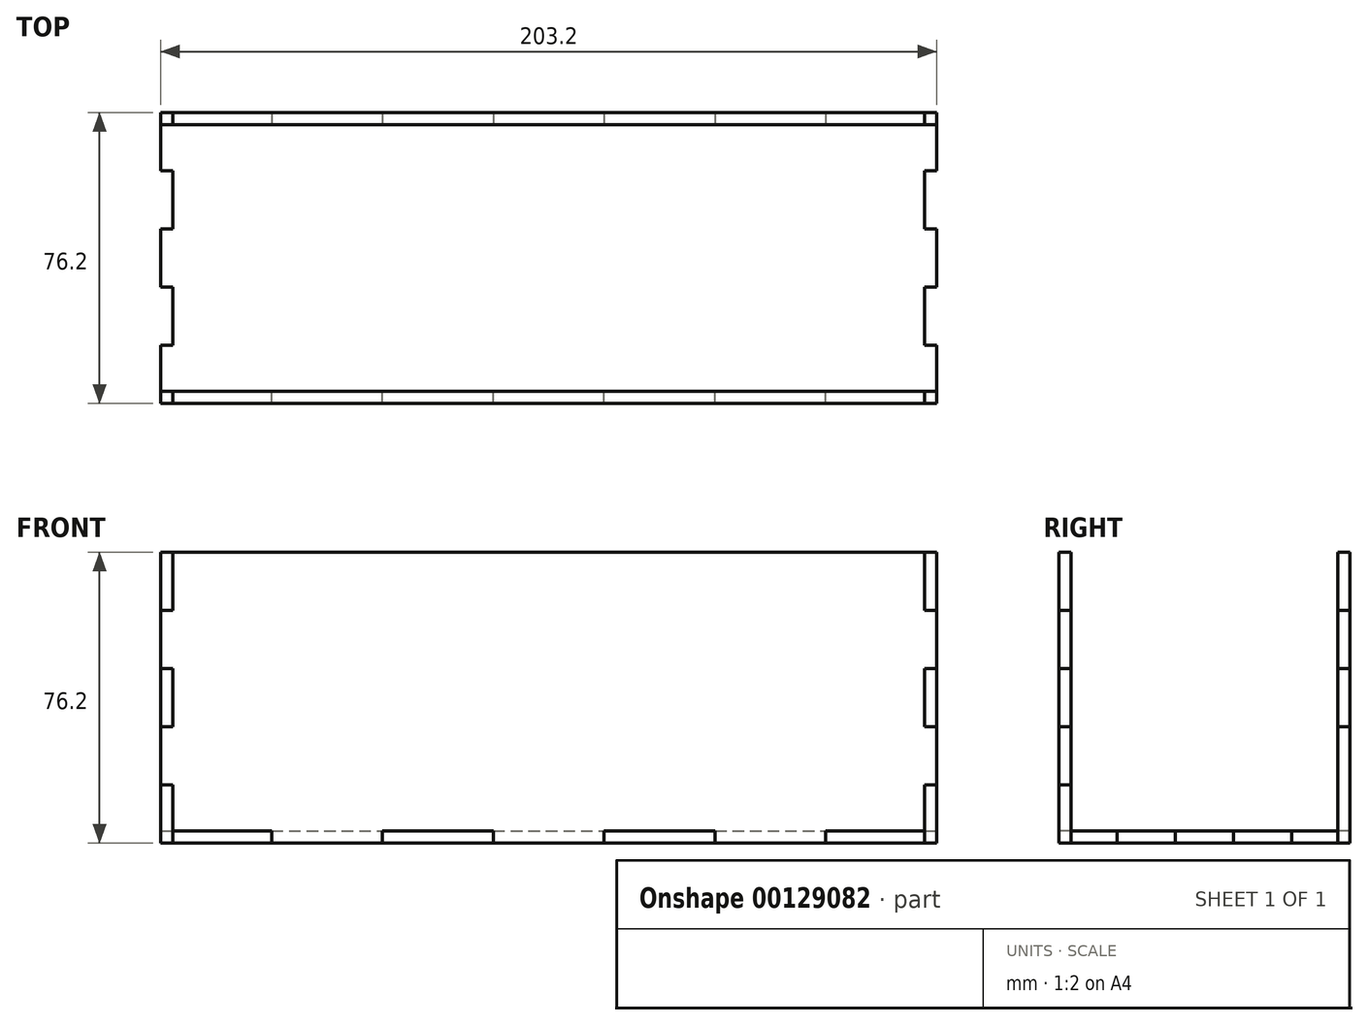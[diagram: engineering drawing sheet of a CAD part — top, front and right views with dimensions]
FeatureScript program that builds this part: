
annotation { "Feature Type Name" : "Feature", "Feature Type Description" : "" }
export const myFeature = defineFeature(function(context is Context, id is Id, definition is map)
    precondition{}
    {
        {
            var Q0;
            Q0=qCreatedBy(makeId("Top.planeOp"),FACE);
            var sketch = newSketch(context, id + "F0", { "sketchPlane" : qUnion([Q0])});
            skLineSegment(sketch, "E0.bottom", {"start": v(101.6, 38.1) * mm, "end": v(-101.6, 38.1) * mm});
            skLineSegment(sketch, "E0.top", {"start": v(101.6, -38.1) * mm, "end": v(-101.6, -38.1) * mm});
            skLineSegment(sketch, "E0.left", {"start": v(101.6, 38.1) * mm, "end": v(101.6, -38.1) * mm});
            skLineSegment(sketch, "E0.right", {"start": v(-101.6, 38.1) * mm, "end": v(-101.6, -38.1) * mm});
            skPoint(sketch, "E0.middle", {"position": v(0, 0) * mm});
            skLineSegment(sketch, "E1", {"start": v(-101.6, 38.1) * mm, "end": v(-98.43, 38.1) * mm});
            skLineSegment(sketch, "E2.0.1.0", {"start": v(-101.6, 22.86) * mm, "end": v(-98.43, 22.86) * mm});
            skLineSegment(sketch, "E2.0.2.0", {"start": v(-101.6, 7.62) * mm, "end": v(-98.43, 7.62) * mm});
            skLineSegment(sketch, "E2.0.3.0", {"start": v(-101.6, -7.62) * mm, "end": v(-98.43, -7.62) * mm});
            skLineSegment(sketch, "E2.0.4.0", {"start": v(-101.6, -22.86) * mm, "end": v(-98.43, -22.86) * mm});
            skLineSegment(sketch, "E2.0.5.0", {"start": v(-101.6, -38.1) * mm, "end": v(-98.43, -38.1) * mm});
            skLineSegment(sketch, "E2.direction1", {"start": v(-101.6, 38.1) * mm, "end": v(-50.8, 38.1) * mm, "construction": true});
            skLineSegment(sketch, "E2.direction2", {"start": v(-101.6, 38.1) * mm, "end": v(-101.6, 22.86) * mm, "construction": true});
            skLineSegment(sketch, "E3", {"start": v(-98.43, 38.1) * mm, "end": v(-98.43, -38.1) * mm});
            skLineSegment(sketch, "E4.MirrorCS", {"start": v(101.6, 38.1) * mm, "end": v(98.43, 38.1) * mm});
            skLineSegment(sketch, "E5.MirrorCS", {"start": v(101.6, -38.1) * mm, "end": v(98.43, -38.1) * mm});
            skLineSegment(sketch, "E6.MirrorCS", {"start": v(101.6, 22.86) * mm, "end": v(98.43, 22.86) * mm});
            skLineSegment(sketch, "E7.MirrorCS", {"start": v(101.6, 7.62) * mm, "end": v(98.43, 7.62) * mm});
            skLineSegment(sketch, "E8.MirrorCS", {"start": v(101.6, -7.62) * mm, "end": v(98.43, -7.62) * mm});
            skLineSegment(sketch, "E9.MirrorCS", {"start": v(101.6, -22.86) * mm, "end": v(98.43, -22.86) * mm});
            skLineSegment(sketch, "E10.MirrorCS", {"start": v(98.43, 38.1) * mm, "end": v(98.43, -38.1) * mm});
            skLineSegment(sketch, "E11.MirrorCS", {"start": v(101.6, 38.1) * mm, "end": v(101.6, 22.86) * mm, "construction": true});
            skLineSegment(sketch, "E12", {"start": v(-101.6, 38.1) * mm, "end": v(-101.6, 34.93) * mm});
            skLineSegment(sketch, "E13.1.0.0", {"start": v(-72.57, 38.1) * mm, "end": v(-72.57, 34.93) * mm});
            skLineSegment(sketch, "E13.2.0.0", {"start": v(-43.54, 38.1) * mm, "end": v(-43.54, 34.93) * mm});
            skLineSegment(sketch, "E13.3.0.0", {"start": v(-14.51, 38.1) * mm, "end": v(-14.51, 34.93) * mm});
            skLineSegment(sketch, "E13.4.0.0", {"start": v(14.51, 38.1) * mm, "end": v(14.51, 34.93) * mm});
            skLineSegment(sketch, "E13.5.0.0", {"start": v(43.54, 38.1) * mm, "end": v(43.54, 34.93) * mm});
            skLineSegment(sketch, "E13.6.0.0", {"start": v(72.57, 38.1) * mm, "end": v(72.57, 34.93) * mm});
            skLineSegment(sketch, "E13.7.0.0", {"start": v(101.6, 38.1) * mm, "end": v(101.6, 34.93) * mm});
            skLineSegment(sketch, "E13.direction1", {"start": v(-101.6, 34.92) * mm, "end": v(-72.57, 34.92) * mm, "construction": true});
            skLineSegment(sketch, "E14", {"start": v(-101.6, 34.92) * mm, "end": v(101.6, 34.93) * mm});
            skLineSegment(sketch, "E15.MirrorCS", {"start": v(-101.6, -38.1) * mm, "end": v(-101.6, -34.93) * mm});
            skLineSegment(sketch, "E16.MirrorCS", {"start": v(101.6, -38.1) * mm, "end": v(101.6, -34.93) * mm});
            skLineSegment(sketch, "E17.MirrorCS", {"start": v(-72.57, -38.1) * mm, "end": v(-72.57, -34.93) * mm});
            skLineSegment(sketch, "E18.MirrorCS", {"start": v(-14.51, -38.1) * mm, "end": v(-14.51, -34.93) * mm});
            skLineSegment(sketch, "E19.MirrorCS", {"start": v(43.54, -38.1) * mm, "end": v(43.54, -34.93) * mm});
            skLineSegment(sketch, "E20.MirrorCS", {"start": v(14.51, -38.1) * mm, "end": v(14.51, -34.93) * mm});
            skLineSegment(sketch, "E21.MirrorCS", {"start": v(-43.54, -38.1) * mm, "end": v(-43.54, -34.93) * mm});
            skLineSegment(sketch, "E22.MirrorCS", {"start": v(72.57, -38.1) * mm, "end": v(72.57, -34.93) * mm});
            skLineSegment(sketch, "E23.MirrorCS", {"start": v(-101.6, -34.93) * mm, "end": v(101.6, -34.92) * mm});
            skLineSegment(sketch, "E24.MirrorCS", {"start": v(-101.6, -38.1) * mm, "end": v(-50.8, -38.1) * mm, "construction": true});
            skLineSegment(sketch, "E25.MirrorCS", {"start": v(-101.6, -34.93) * mm, "end": v(-72.57, -34.93) * mm, "construction": true});
            skSolve(sketch);
        }
        {
            var Q0;
            {var subQ0=sQuery(id+"F0.wireOp",EDGE,"E1");Q0=makeQuery(id+"F0.imprint","IMPRINT",FACE,{"disambiguationData":[TD([[makeQuery(id+"F0.imprint","IMPRINT",EDGE,{"derivedFrom":subQ0}),-1.0]])]});}
            var Q1;
            {var subQ3=sQuery(id+"F0.wireOp",EDGE,"E2.0.1.0");Q1=makeQuery(id+"F0.imprint","IMPRINT",FACE,{"disambiguationData":[TD([[makeQuery(id+"F0.imprint","IMPRINT",EDGE,{"derivedFrom":subQ3}),1.0]])]});}
            var Q2;
            {var subQ3=sQuery(id+"F0.wireOp",EDGE,"E13.1.0.0");Q2=makeQuery(id+"F0.imprint","IMPRINT",FACE,{"disambiguationData":[TD([[makeQuery(id+"F0.imprint","IMPRINT",EDGE,{"derivedFrom":subQ3}),-1.0]])]});}
            var Q3;
            {var subQ5=sQuery(id+"F0.wireOp",EDGE,"E3");var subQ23=makeQuery(id+"F0.imprint","INTERSECT",VERTEX,{"derivedFrom":[sQuery(id+"F0.wireOp",EDGE,"E2.0.1.0"),subQ5]});Q3=makeQuery(id+"F0.imprint","IMPRINT",FACE,{"disambiguationData":[TD([[makeQuery(id+"F0.imprint","IMPRINT",EDGE,{"disambiguationData":[TD([[subQ23,1.0]])],"derivedFrom":subQ5}),1.0]])]});}
            var Q4;
            {var subQ0=sQuery(id+"F0.wireOp",EDGE,"E2.0.2.0");Q4=makeQuery(id+"F0.imprint","IMPRINT",FACE,{"disambiguationData":[TD([[makeQuery(id+"F0.imprint","IMPRINT",EDGE,{"derivedFrom":subQ0}),-1.0]])]});}
            var Q5;
            {var subQ3=sQuery(id+"F0.wireOp",EDGE,"E2.0.4.0");Q5=makeQuery(id+"F0.imprint","IMPRINT",FACE,{"disambiguationData":[TD([[makeQuery(id+"F0.imprint","IMPRINT",EDGE,{"derivedFrom":subQ3}),-1.0]])]});}
            var Q6;
            {var subQ5=sQuery(id+"F0.wireOp",EDGE,"E15.MirrorCS");Q6=makeQuery(id+"F0.imprint","IMPRINT",FACE,{"disambiguationData":[TD([[makeQuery(id+"F0.imprint","IMPRINT",EDGE,{"derivedFrom":subQ5}),-1.0]])]});}
            var Q7;
            {var subQ5=sQuery(id+"F0.wireOp",EDGE,"E17.MirrorCS");Q7=makeQuery(id+"F0.imprint","IMPRINT",FACE,{"disambiguationData":[TD([[makeQuery(id+"F0.imprint","IMPRINT",EDGE,{"derivedFrom":subQ5}),1.0]])]});}
            var Q8;
            {var subQ0=sQuery(id+"F0.wireOp",EDGE,"E18.MirrorCS");Q8=makeQuery(id+"F0.imprint","IMPRINT",FACE,{"disambiguationData":[TD([[makeQuery(id+"F0.imprint","IMPRINT",EDGE,{"derivedFrom":subQ0}),1.0]])]});}
            var Q9;
            {var subQ0=sQuery(id+"F0.wireOp",EDGE,"E19.MirrorCS");Q9=makeQuery(id+"F0.imprint","IMPRINT",FACE,{"disambiguationData":[TD([[makeQuery(id+"F0.imprint","IMPRINT",EDGE,{"derivedFrom":subQ0}),1.0]])]});}
            var Q10;
            {var subQ5=sQuery(id+"F0.wireOp",EDGE,"E22.MirrorCS");Q10=makeQuery(id+"F0.imprint","IMPRINT",FACE,{"disambiguationData":[TD([[makeQuery(id+"F0.imprint","IMPRINT",EDGE,{"derivedFrom":subQ5}),-1.0]])]});}
            var Q11;
            {var subQ5=sQuery(id+"F0.wireOp",EDGE,"E16.MirrorCS");Q11=makeQuery(id+"F0.imprint","IMPRINT",FACE,{"disambiguationData":[TD([[makeQuery(id+"F0.imprint","IMPRINT",EDGE,{"derivedFrom":subQ5}),1.0]])]});}
            var Q12;
            {var subQ0=sQuery(id+"F0.wireOp",EDGE,"E9.MirrorCS");Q12=makeQuery(id+"F0.imprint","IMPRINT",FACE,{"disambiguationData":[TD([[makeQuery(id+"F0.imprint","IMPRINT",EDGE,{"derivedFrom":subQ0}),1.0]])]});}
            var Q13;
            {var subQ0=sQuery(id+"F0.wireOp",EDGE,"E7.MirrorCS");Q13=makeQuery(id+"F0.imprint","IMPRINT",FACE,{"disambiguationData":[TD([[makeQuery(id+"F0.imprint","IMPRINT",EDGE,{"derivedFrom":subQ0}),1.0]])]});}
            var Q14;
            {var subQ0=sQuery(id+"F0.wireOp",EDGE,"E6.MirrorCS");Q14=makeQuery(id+"F0.imprint","IMPRINT",FACE,{"disambiguationData":[TD([[makeQuery(id+"F0.imprint","IMPRINT",EDGE,{"derivedFrom":subQ0}),-1.0]])]});}
            var Q15;
            {var subQ0=sQuery(id+"F0.wireOp",EDGE,"E4.MirrorCS");Q15=makeQuery(id+"F0.imprint","IMPRINT",FACE,{"disambiguationData":[TD([[makeQuery(id+"F0.imprint","IMPRINT",EDGE,{"derivedFrom":subQ0}),1.0]])]});}
            var Q16;
            {var subQ3=sQuery(id+"F0.wireOp",EDGE,"E13.6.0.0");Q16=makeQuery(id+"F0.imprint","IMPRINT",FACE,{"disambiguationData":[TD([[makeQuery(id+"F0.imprint","IMPRINT",EDGE,{"derivedFrom":subQ3}),1.0]])]});}
            var Q17;
            {var subQ0=sQuery(id+"F0.wireOp",EDGE,"E13.4.0.0");Q17=makeQuery(id+"F0.imprint","IMPRINT",FACE,{"disambiguationData":[TD([[makeQuery(id+"F0.imprint","IMPRINT",EDGE,{"derivedFrom":subQ0}),1.0]])]});}
            var Q18;
            {var subQ0=sQuery(id+"F0.wireOp",EDGE,"E13.2.0.0");Q18=makeQuery(id+"F0.imprint","IMPRINT",FACE,{"disambiguationData":[TD([[makeQuery(id+"F0.imprint","IMPRINT",EDGE,{"derivedFrom":subQ0}),1.0]])]});}
            extrude(context, id + "F1", {"entities" : qUnion([Q0, Q1, Q2, Q3, Q4, Q5, Q6, Q7, Q8, Q9, Q10, Q11, Q12, Q13, Q14, Q15, Q16, Q17, Q18]), "depth" : 3.17 * mm});
        }
        {
            var Q0;
            Q0=makeQuery(id+"F1.opExtrude","SWEPT_FACE",FACE,{"disambiguationData":[OSD([sQuery(id+"F0.wireOp",EDGE,"E0.left"),sQuery(id+"F0.wireOp",EDGE,"E16.MirrorCS")])]});
            var sketch = newSketch(context, id + "F2", { "sketchPlane" : qUnion([Q0])});
            skLineSegment(sketch, "E26.bottom", {"start": v(-38.1, 0) * mm, "end": v(38.1, 0) * mm});
            skLineSegment(sketch, "E26.top", {"start": v(-38.1, 76.2) * mm, "end": v(38.1, 76.2) * mm});
            skLineSegment(sketch, "E26.left", {"start": v(-38.1, 0) * mm, "end": v(-38.1, 76.2) * mm});
            skLineSegment(sketch, "E26.right", {"start": v(38.1, 0) * mm, "end": v(38.1, 76.2) * mm});
            skLineSegment(sketch, "E27", {"start": v(-38.1, 76.2) * mm, "end": v(-34.93, 76.2) * mm});
            skLineSegment(sketch, "E28.0.1.0", {"start": v(-38.1, 60.96) * mm, "end": v(-34.93, 60.96) * mm});
            skLineSegment(sketch, "E28.0.2.0", {"start": v(-38.1, 45.72) * mm, "end": v(-34.93, 45.72) * mm});
            skLineSegment(sketch, "E28.0.3.0", {"start": v(-38.1, 30.48) * mm, "end": v(-34.93, 30.48) * mm});
            skLineSegment(sketch, "E28.0.4.0", {"start": v(-38.1, 15.24) * mm, "end": v(-34.93, 15.24) * mm});
            skLineSegment(sketch, "E28.0.5.0", {"start": v(-38.1, 0) * mm, "end": v(-34.93, 0) * mm});
            skLineSegment(sketch, "E28.direction1", {"start": v(-38.1, 76.2) * mm, "end": v(-25.4, 76.2) * mm, "construction": true});
            skLineSegment(sketch, "E28.direction2", {"start": v(-38.1, 76.2) * mm, "end": v(-38.1, 60.96) * mm, "construction": true});
            skLineSegment(sketch, "E29", {"start": v(-34.93, 76.2) * mm, "end": v(-34.93, 0) * mm});
            skLineSegment(sketch, "E30.MirrorCS", {"start": v(38.1, 76.2) * mm, "end": v(34.92, 76.2) * mm});
            skLineSegment(sketch, "E31.MirrorCS", {"start": v(38.1, 0) * mm, "end": v(34.93, 0) * mm});
            skLineSegment(sketch, "E32.MirrorCS", {"start": v(38.1, 60.96) * mm, "end": v(34.92, 60.96) * mm});
            skLineSegment(sketch, "E33.MirrorCS", {"start": v(38.1, 30.48) * mm, "end": v(34.93, 30.48) * mm});
            skLineSegment(sketch, "E34.MirrorCS", {"start": v(38.1, 15.24) * mm, "end": v(34.93, 15.24) * mm});
            skLineSegment(sketch, "E35.MirrorCS", {"start": v(38.1, 45.72) * mm, "end": v(34.93, 45.72) * mm});
            skLineSegment(sketch, "E36.MirrorCS", {"start": v(38.1, 76.2) * mm, "end": v(38.1, 60.96) * mm, "construction": true});
            skLineSegment(sketch, "E37.MirrorCS", {"start": v(34.93, 76.2) * mm, "end": v(34.93, 0) * mm});
            skSolve(sketch);
        }
        {
            var Q0;
            {var subQ3=sQuery(id+"F2.wireOp",EDGE,"E26.top");Q0=makeQuery(id+"F2.imprint","IMPRINT",FACE,{"disambiguationData":[TD([[makeQuery(id+"F2.imprint","IMPRINT",EDGE,{"derivedFrom":subQ3}),-1.0]])]});}
            var Q1;
            {var subQ0=sQuery(id+"F2.wireOp",EDGE,"E27");Q1=makeQuery(id+"F2.imprint","IMPRINT",FACE,{"disambiguationData":[TD([[makeQuery(id+"F2.imprint","IMPRINT",EDGE,{"derivedFrom":subQ0}),-1.0]])]});}
            var Q2;
            {var subQ0=sQuery(id+"F2.wireOp",EDGE,"E28.0.2.0");Q2=makeQuery(id+"F2.imprint","IMPRINT",FACE,{"disambiguationData":[TD([[makeQuery(id+"F2.imprint","IMPRINT",EDGE,{"derivedFrom":subQ0}),-1.0]])]});}
            var Q3;
            {var subQ3=sQuery(id+"F2.wireOp",EDGE,"E28.0.4.0");Q3=makeQuery(id+"F2.imprint","IMPRINT",FACE,{"disambiguationData":[TD([[makeQuery(id+"F2.imprint","IMPRINT",EDGE,{"derivedFrom":subQ3}),-1.0]])]});}
            var Q4;
            {var subQ0=sQuery(id+"F2.wireOp",EDGE,"E28.0.5.0");Q4=makeQuery(id+"F2.imprint","IMPRINT",FACE,{"disambiguationData":[TD([[makeQuery(id+"F2.imprint","IMPRINT",EDGE,{"derivedFrom":subQ0}),1.0]])]});}
            var Q5;
            {var subQ1=sQuery(id+"F0.wireOp",EDGE,"E0.left");var subQ2=makeQuery(id+"F1.opExtrude","SWEPT_EDGE",EDGE,{"disambiguationData":[OSD([sQuery(id+"F0.wireOp",EDGE,"E9.MirrorCS"),subQ1])]});Q5=makeQuery(id+"F2.imprint","IMPRINT",FACE,{"disambiguationData":[TD([[makeQuery(id+"F2.imprint","IMPRINT",EDGE,{"derivedFrom":subQ2}),-1.0]])]});}
            var Q6;
            {var subQ0=sQuery(id+"F2.wireOp",EDGE,"E31.MirrorCS");Q6=makeQuery(id+"F2.imprint","IMPRINT",FACE,{"disambiguationData":[TD([[makeQuery(id+"F2.imprint","IMPRINT",EDGE,{"derivedFrom":subQ0}),-1.0]])]});}
            var Q7;
            {var subQ0=sQuery(id+"F2.wireOp",EDGE,"E33.MirrorCS");Q7=makeQuery(id+"F2.imprint","IMPRINT",FACE,{"disambiguationData":[TD([[makeQuery(id+"F2.imprint","IMPRINT",EDGE,{"derivedFrom":subQ0}),-1.0]])]});}
            var Q8;
            {var subQ0=sQuery(id+"F2.wireOp",EDGE,"E30.MirrorCS");Q8=makeQuery(id+"F2.imprint","IMPRINT",FACE,{"disambiguationData":[TD([[makeQuery(id+"F2.imprint","IMPRINT",EDGE,{"derivedFrom":subQ0}),1.0]])]});}
            extrude(context, id + "F3", {"entities" : qUnion([Q0, Q1, Q2, Q3, Q4, Q5, Q6, Q7, Q8]), "oppositeDirection" : true, "depth" : 3.17 * mm});
        }
        {
            var Q0;
            Q0=makeQuery(id+"F3.opExtrude","SWEPT_BODY",BODY,{"disambiguationData":[OSD([sQuery(id+"F2.wireOp",EDGE,"E26.bottom"),sQuery(id+"F2.wireOp",EDGE,"E26.top"),sQuery(id+"F2.wireOp",EDGE,"E26.left"),sQuery(id+"F2.wireOp",EDGE,"E27"),sQuery(id+"F2.wireOp",EDGE,"E28.0.1.0"),sQuery(id+"F2.wireOp",EDGE,"E28.0.2.0"),sQuery(id+"F2.wireOp",EDGE,"E28.0.3.0"),sQuery(id+"F2.wireOp",EDGE,"E28.0.4.0"),sQuery(id+"F2.wireOp",EDGE,"E28.0.5.0"),sQuery(id+"F2.wireOp",EDGE,"E29"),sQuery(id+"F2.wireOp",EDGE,"E30.MirrorCS"),sQuery(id+"F2.wireOp",EDGE,"E31.MirrorCS"),sQuery(id+"F2.wireOp",EDGE,"E32.MirrorCS"),sQuery(id+"F2.wireOp",EDGE,"E33.MirrorCS"),sQuery(id+"F2.wireOp",EDGE,"E34.MirrorCS"),sQuery(id+"F2.wireOp",EDGE,"E35.MirrorCS"),sQuery(id+"F2.wireOp",EDGE,"E26.right"),sQuery(id+"F2.wireOp",EDGE,"E37.MirrorCS")])]});
            var Q1;
            Q1=qCreatedBy(makeId("Right.planeOp"),FACE);
            mirror(context, id + "F4", {"entities" : qUnion([Q0]), "mirrorPlane" : qUnion([Q1])});
        }
        {
            var Q0;
            Q0=makeQuery(id+"F1.opExtrude","SWEPT_BODY",BODY,{"disambiguationData":[OSD([sQuery(id+"F0.wireOp",EDGE,"E0.bottom"),sQuery(id+"F0.wireOp",EDGE,"E0.right"),sQuery(id+"F0.wireOp",EDGE,"E1"),sQuery(id+"F0.wireOp",EDGE,"E2.0.1.0"),sQuery(id+"F0.wireOp",EDGE,"E2.0.2.0"),sQuery(id+"F0.wireOp",EDGE,"E2.0.3.0"),sQuery(id+"F0.wireOp",EDGE,"E2.0.4.0"),sQuery(id+"F0.wireOp",EDGE,"E3"),sQuery(id+"F0.wireOp",EDGE,"E4.MirrorCS"),sQuery(id+"F0.wireOp",EDGE,"E6.MirrorCS"),sQuery(id+"F0.wireOp",EDGE,"E7.MirrorCS"),sQuery(id+"F0.wireOp",EDGE,"E8.MirrorCS"),sQuery(id+"F0.wireOp",EDGE,"E9.MirrorCS"),sQuery(id+"F0.wireOp",EDGE,"E10.MirrorCS"),sQuery(id+"F0.wireOp",EDGE,"E0.left"),sQuery(id+"F0.wireOp",EDGE,"E12"),sQuery(id+"F0.wireOp",EDGE,"E13.1.0.0"),sQuery(id+"F0.wireOp",EDGE,"E13.2.0.0"),sQuery(id+"F0.wireOp",EDGE,"E13.3.0.0"),sQuery(id+"F0.wireOp",EDGE,"E13.4.0.0"),sQuery(id+"F0.wireOp",EDGE,"E13.5.0.0"),sQuery(id+"F0.wireOp",EDGE,"E13.6.0.0"),sQuery(id+"F0.wireOp",EDGE,"E13.7.0.0"),sQuery(id+"F0.wireOp",EDGE,"E14"),sQuery(id+"F0.wireOp",EDGE,"E15.MirrorCS"),sQuery(id+"F0.wireOp",EDGE,"E16.MirrorCS"),sQuery(id+"F0.wireOp",EDGE,"E17.MirrorCS"),sQuery(id+"F0.wireOp",EDGE,"E18.MirrorCS"),sQuery(id+"F0.wireOp",EDGE,"E19.MirrorCS"),sQuery(id+"F0.wireOp",EDGE,"E20.MirrorCS"),sQuery(id+"F0.wireOp",EDGE,"E21.MirrorCS"),sQuery(id+"F0.wireOp",EDGE,"E22.MirrorCS"),sQuery(id+"F0.wireOp",EDGE,"E23.MirrorCS"),sQuery(id+"F0.wireOp",EDGE,"E0.top")])]});
            var Q1;
            Q1=makeQuery(id+"F3.opExtrude","SWEPT_BODY",BODY,{"disambiguationData":[OSD([sQuery(id+"F2.wireOp",EDGE,"E26.bottom"),sQuery(id+"F2.wireOp",EDGE,"E26.top"),sQuery(id+"F2.wireOp",EDGE,"E26.left"),sQuery(id+"F2.wireOp",EDGE,"E27"),sQuery(id+"F2.wireOp",EDGE,"E28.0.1.0"),sQuery(id+"F2.wireOp",EDGE,"E28.0.2.0"),sQuery(id+"F2.wireOp",EDGE,"E28.0.3.0"),sQuery(id+"F2.wireOp",EDGE,"E28.0.4.0"),sQuery(id+"F2.wireOp",EDGE,"E28.0.5.0"),sQuery(id+"F2.wireOp",EDGE,"E29"),sQuery(id+"F2.wireOp",EDGE,"E30.MirrorCS"),sQuery(id+"F2.wireOp",EDGE,"E31.MirrorCS"),sQuery(id+"F2.wireOp",EDGE,"E32.MirrorCS"),sQuery(id+"F2.wireOp",EDGE,"E33.MirrorCS"),sQuery(id+"F2.wireOp",EDGE,"E34.MirrorCS"),sQuery(id+"F2.wireOp",EDGE,"E35.MirrorCS"),sQuery(id+"F2.wireOp",EDGE,"E26.right"),sQuery(id+"F2.wireOp",EDGE,"E37.MirrorCS")])]});
            var Q2;
            Q2=makeQuery(id+"F4.opPattern","COPY",BODY,{"derivedFrom":makeQuery(id+"F3.opExtrude","SWEPT_BODY",BODY,{"disambiguationData":[OSD([sQuery(id+"F2.wireOp",EDGE,"E26.bottom"),sQuery(id+"F2.wireOp",EDGE,"E26.top"),sQuery(id+"F2.wireOp",EDGE,"E26.left"),sQuery(id+"F2.wireOp",EDGE,"E27"),sQuery(id+"F2.wireOp",EDGE,"E28.0.1.0"),sQuery(id+"F2.wireOp",EDGE,"E28.0.2.0"),sQuery(id+"F2.wireOp",EDGE,"E28.0.3.0"),sQuery(id+"F2.wireOp",EDGE,"E28.0.4.0"),sQuery(id+"F2.wireOp",EDGE,"E28.0.5.0"),sQuery(id+"F2.wireOp",EDGE,"E29"),sQuery(id+"F2.wireOp",EDGE,"E30.MirrorCS"),sQuery(id+"F2.wireOp",EDGE,"E31.MirrorCS"),sQuery(id+"F2.wireOp",EDGE,"E32.MirrorCS"),sQuery(id+"F2.wireOp",EDGE,"E33.MirrorCS"),sQuery(id+"F2.wireOp",EDGE,"E34.MirrorCS"),sQuery(id+"F2.wireOp",EDGE,"E35.MirrorCS"),sQuery(id+"F2.wireOp",EDGE,"E26.right"),sQuery(id+"F2.wireOp",EDGE,"E37.MirrorCS")])]}),"instanceName":"1"});
            booleanBodies(context, id + "F5", {"operationType" : BooleanOperationType.SUBTRACTION, "tools" : qUnion([Q0]), "targets" : qUnion([Q1, Q2]), "keepTools" : true});
        }
        {
            var Q0;
            Q0=makeQuery(id+"F1.opExtrude","SWEPT_FACE",FACE,{"disambiguationData":[OSD([sQuery(id+"F0.wireOp",EDGE,"E0.bottom"),sQuery(id+"F0.wireOp",EDGE,"E4.MirrorCS")])]});
            var sketch = newSketch(context, id + "F6", { "sketchPlane" : qUnion([Q0])});
            skLineSegment(sketch, "E38.bottom", {"start": v(-101.6, 0) * mm, "end": v(101.6, 0) * mm});
            skLineSegment(sketch, "E38.top", {"start": v(-101.6, 76.2) * mm, "end": v(101.6, 76.2) * mm});
            skLineSegment(sketch, "E38.left", {"start": v(-101.6, 0) * mm, "end": v(-101.6, 76.2) * mm});
            skLineSegment(sketch, "E38.right", {"start": v(101.6, 0) * mm, "end": v(101.6, 76.2) * mm});
            skSolve(sketch);
        }
        {
            var Q0;
            {var subQ4=sQuery(id+"F6.wireOp",EDGE,"E38.top");Q0=makeQuery(id+"F6.imprint","IMPRINT",FACE,{"disambiguationData":[TD([[makeQuery(id+"F6.imprint","IMPRINT",EDGE,{"derivedFrom":subQ4}),-1.0]])]});}
            extrude(context, id + "F7", {"entities" : qUnion([Q0]), "oppositeDirection" : true, "depth" : 3.17 * mm});
        }
        {
            var Q0;
            Q0=makeQuery(id+"F7.opExtrude","SWEPT_BODY",BODY,{"disambiguationData":[OSD([sQuery(id+"F0.wireOp",EDGE,"E0.bottom"),sQuery(id+"F0.wireOp",EDGE,"E4.MirrorCS"),sQuery(id+"F0.wireOp",EDGE,"E13.6.0.0"),sQuery(id+"F6.wireOp",EDGE,"E38.bottom"),sQuery(id+"F6.wireOp",EDGE,"E38.top"),sQuery(id+"F6.wireOp",EDGE,"E38.left"),sQuery(id+"F6.wireOp",EDGE,"E38.right")])]});
            var Q1;
            Q1=qCreatedBy(makeId("Front.planeOp"),FACE);
            mirror(context, id + "F8", {"entities" : qUnion([Q0]), "mirrorPlane" : qUnion([Q1])});
        }
        {
            var Q0;
            Q0=makeQuery(id+"F4.opPattern","COPY",BODY,{"derivedFrom":makeQuery(id+"F3.opExtrude","SWEPT_BODY",BODY,{"disambiguationData":[OSD([sQuery(id+"F2.wireOp",EDGE,"E26.bottom"),sQuery(id+"F2.wireOp",EDGE,"E26.top"),sQuery(id+"F2.wireOp",EDGE,"E26.left"),sQuery(id+"F2.wireOp",EDGE,"E27"),sQuery(id+"F2.wireOp",EDGE,"E28.0.1.0"),sQuery(id+"F2.wireOp",EDGE,"E28.0.2.0"),sQuery(id+"F2.wireOp",EDGE,"E28.0.3.0"),sQuery(id+"F2.wireOp",EDGE,"E28.0.4.0"),sQuery(id+"F2.wireOp",EDGE,"E28.0.5.0"),sQuery(id+"F2.wireOp",EDGE,"E29"),sQuery(id+"F2.wireOp",EDGE,"E30.MirrorCS"),sQuery(id+"F2.wireOp",EDGE,"E31.MirrorCS"),sQuery(id+"F2.wireOp",EDGE,"E32.MirrorCS"),sQuery(id+"F2.wireOp",EDGE,"E33.MirrorCS"),sQuery(id+"F2.wireOp",EDGE,"E34.MirrorCS"),sQuery(id+"F2.wireOp",EDGE,"E35.MirrorCS"),sQuery(id+"F2.wireOp",EDGE,"E26.right"),sQuery(id+"F2.wireOp",EDGE,"E37.MirrorCS")])]}),"instanceName":"1"});
            var Q1;
            Q1=makeQuery(id+"F1.opExtrude","SWEPT_BODY",BODY,{"disambiguationData":[OSD([sQuery(id+"F0.wireOp",EDGE,"E0.bottom"),sQuery(id+"F0.wireOp",EDGE,"E0.right"),sQuery(id+"F0.wireOp",EDGE,"E1"),sQuery(id+"F0.wireOp",EDGE,"E2.0.1.0"),sQuery(id+"F0.wireOp",EDGE,"E2.0.2.0"),sQuery(id+"F0.wireOp",EDGE,"E2.0.3.0"),sQuery(id+"F0.wireOp",EDGE,"E2.0.4.0"),sQuery(id+"F0.wireOp",EDGE,"E3"),sQuery(id+"F0.wireOp",EDGE,"E4.MirrorCS"),sQuery(id+"F0.wireOp",EDGE,"E6.MirrorCS"),sQuery(id+"F0.wireOp",EDGE,"E7.MirrorCS"),sQuery(id+"F0.wireOp",EDGE,"E8.MirrorCS"),sQuery(id+"F0.wireOp",EDGE,"E9.MirrorCS"),sQuery(id+"F0.wireOp",EDGE,"E10.MirrorCS"),sQuery(id+"F0.wireOp",EDGE,"E0.left"),sQuery(id+"F0.wireOp",EDGE,"E12"),sQuery(id+"F0.wireOp",EDGE,"E13.1.0.0"),sQuery(id+"F0.wireOp",EDGE,"E13.2.0.0"),sQuery(id+"F0.wireOp",EDGE,"E13.3.0.0"),sQuery(id+"F0.wireOp",EDGE,"E13.4.0.0"),sQuery(id+"F0.wireOp",EDGE,"E13.5.0.0"),sQuery(id+"F0.wireOp",EDGE,"E13.6.0.0"),sQuery(id+"F0.wireOp",EDGE,"E13.7.0.0"),sQuery(id+"F0.wireOp",EDGE,"E14"),sQuery(id+"F0.wireOp",EDGE,"E15.MirrorCS"),sQuery(id+"F0.wireOp",EDGE,"E16.MirrorCS"),sQuery(id+"F0.wireOp",EDGE,"E17.MirrorCS"),sQuery(id+"F0.wireOp",EDGE,"E18.MirrorCS"),sQuery(id+"F0.wireOp",EDGE,"E19.MirrorCS"),sQuery(id+"F0.wireOp",EDGE,"E20.MirrorCS"),sQuery(id+"F0.wireOp",EDGE,"E21.MirrorCS"),sQuery(id+"F0.wireOp",EDGE,"E22.MirrorCS"),sQuery(id+"F0.wireOp",EDGE,"E23.MirrorCS"),sQuery(id+"F0.wireOp",EDGE,"E0.top")])]});
            var Q2;
            Q2=makeQuery(id+"F3.opExtrude","SWEPT_BODY",BODY,{"disambiguationData":[OSD([sQuery(id+"F2.wireOp",EDGE,"E26.bottom"),sQuery(id+"F2.wireOp",EDGE,"E26.top"),sQuery(id+"F2.wireOp",EDGE,"E26.left"),sQuery(id+"F2.wireOp",EDGE,"E27"),sQuery(id+"F2.wireOp",EDGE,"E28.0.1.0"),sQuery(id+"F2.wireOp",EDGE,"E28.0.2.0"),sQuery(id+"F2.wireOp",EDGE,"E28.0.3.0"),sQuery(id+"F2.wireOp",EDGE,"E28.0.4.0"),sQuery(id+"F2.wireOp",EDGE,"E28.0.5.0"),sQuery(id+"F2.wireOp",EDGE,"E29"),sQuery(id+"F2.wireOp",EDGE,"E30.MirrorCS"),sQuery(id+"F2.wireOp",EDGE,"E31.MirrorCS"),sQuery(id+"F2.wireOp",EDGE,"E32.MirrorCS"),sQuery(id+"F2.wireOp",EDGE,"E33.MirrorCS"),sQuery(id+"F2.wireOp",EDGE,"E34.MirrorCS"),sQuery(id+"F2.wireOp",EDGE,"E35.MirrorCS"),sQuery(id+"F2.wireOp",EDGE,"E26.right"),sQuery(id+"F2.wireOp",EDGE,"E37.MirrorCS")])]});
            var Q3;
            Q3=makeQuery(id+"F8.opPattern","COPY",BODY,{"derivedFrom":makeQuery(id+"F7.opExtrude","SWEPT_BODY",BODY,{"disambiguationData":[OSD([sQuery(id+"F0.wireOp",EDGE,"E0.bottom"),sQuery(id+"F0.wireOp",EDGE,"E4.MirrorCS"),sQuery(id+"F0.wireOp",EDGE,"E13.6.0.0"),sQuery(id+"F6.wireOp",EDGE,"E38.bottom"),sQuery(id+"F6.wireOp",EDGE,"E38.top"),sQuery(id+"F6.wireOp",EDGE,"E38.left"),sQuery(id+"F6.wireOp",EDGE,"E38.right")])]}),"instanceName":"1"});
            var Q4;
            Q4=makeQuery(id+"F7.opExtrude","SWEPT_BODY",BODY,{"disambiguationData":[OSD([sQuery(id+"F0.wireOp",EDGE,"E0.bottom"),sQuery(id+"F0.wireOp",EDGE,"E4.MirrorCS"),sQuery(id+"F0.wireOp",EDGE,"E13.6.0.0"),sQuery(id+"F6.wireOp",EDGE,"E38.bottom"),sQuery(id+"F6.wireOp",EDGE,"E38.top"),sQuery(id+"F6.wireOp",EDGE,"E38.left"),sQuery(id+"F6.wireOp",EDGE,"E38.right")])]});
            booleanBodies(context, id + "F9", {"operationType" : BooleanOperationType.SUBTRACTION, "tools" : qUnion([Q0, Q1, Q2]), "targets" : qUnion([Q3, Q4]), "keepTools" : true});
        }
    });
